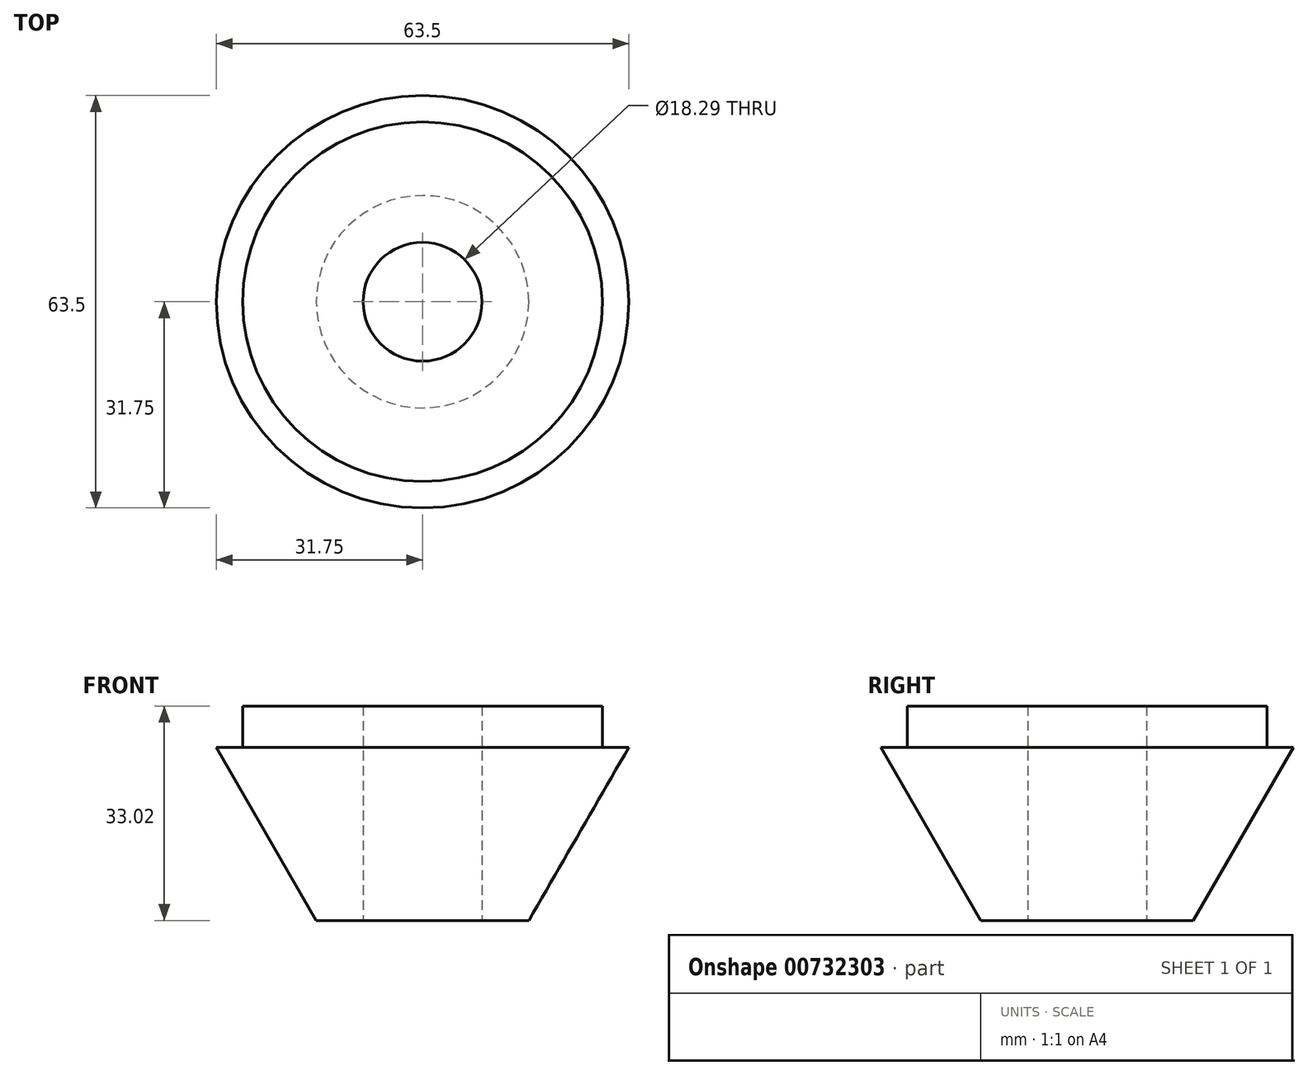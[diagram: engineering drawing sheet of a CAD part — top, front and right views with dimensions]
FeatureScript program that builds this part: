
annotation { "Feature Type Name" : "Feature", "Feature Type Description" : "" }
export const myFeature = defineFeature(function(context is Context, id is Id, definition is map)
    precondition{}
    {
        {
            var Q0;
            Q0=qCreatedBy(makeId("Top.planeOp"),FACE);
            var sketch = newSketch(context, id + "F0", { "sketchPlane" : qUnion([Q0])});
            skCircle(sketch, "E0", {"center": v(0, 0) * mm, "radius": 27.69 * mm});
            skSolve(sketch);
        }
        {
            var Q0;
            Q0=makeQuery(id+"F0.imprint","IMPRINT",FACE,{"disambiguationData":[TD([[makeQuery(id+"F0.imprint","IMPRINT",EDGE,{"derivedFrom":sQuery(id+"F0.wireOp",EDGE,"E0")}),1.0]])]});
            extrude(context, id + "F1", {"entities" : qUnion([Q0]), "depth" : 6.35 * mm, "offsetDistance" : 25.4 * mm});
        }
        {
            var Q0;
            Q0=sQuery(id+"F0.wireOp",VERTEX,"E0.center");
            var Q1;
            Q1=makeQuery(id+"F1.opExtrude","SWEPT_BODY",BODY,{"disambiguationData":[OSD([sQuery(id+"F0.wireOp",EDGE,"E0")])]});
            hole(context, id + "F2", {"style" : HoleStyle.SIMPLE, "endStyle" : HoleEndStyle.THROUGH, "oppositeDirection" : true, "holeDiameter" : 18.29 * mm, "majorDiameter" : 6.35 * mm, "isTappedThrough" : true, "tappedDepth" : 12.7 * mm, "tapClearance" : 3, "locations" : qUnion([Q0]), "scope" : qUnion([Q1])});
        }
        {
            var Q0;
            Q0=qCreatedBy(makeId("Top.planeOp"),FACE);
            var sketch = newSketch(context, id + "F3", { "sketchPlane" : qUnion([Q0])});
            skCircle(sketch, "E1", {"center": v(0, 0) * mm, "radius": 31.75 * mm});
            skSolve(sketch);
        }
        {
            var Q0;
            Q0=qCreatedBy(makeId("Top.planeOp"),FACE);
            cPlane(context, id + "F4", {"entities" : qUnion([Q0]), "cplaneType" : CPlaneType.OFFSET, "offset" : 26.67 * mm, "oppositeDirection" : true, "width" : 152.4 * mm, "height" : 152.4 * mm});
        }
        {
            var Q0;
            Q0=qSketchRegion(id+"F3",true);
            extrude(context, id + "F5", {"entities" : qUnion([Q0]), "operationType" : NewBodyOperationType.ADD, "oppositeDirection" : true, "depth" : 26.67 * mm, "offsetDistance" : 25.4 * mm, "hasDraft" : true, "draftAngle" : 30 * degree, "draftPullDirection" : true});
        }
        {
            var Q0;
            Q0=qCreatedBy(id+"F4.planeOp",FACE);
            var sketch = newSketch(context, id + "F6", { "sketchPlane" : qUnion([Q0])});
            skPoint(sketch, "E2", {"position": v(0, 0) * mm});
            skSolve(sketch);
        }
        {
            var Q0;
            Q0=sQuery(id+"F6.wireOp",VERTEX,"E2");
            var Q1;
            Q1=makeQuery(id+"F1.opExtrude","SWEPT_BODY",BODY,{"disambiguationData":[OSD([sQuery(id+"F0.wireOp",EDGE,"E0")])]});
            hole(context, id + "F7", {"style" : HoleStyle.SIMPLE, "endStyle" : HoleEndStyle.THROUGH, "oppositeDirection" : true, "holeDiameter" : 18.29 * mm, "majorDiameter" : 6.35 * mm, "isTappedThrough" : true, "tappedDepth" : 12.7 * mm, "tapClearance" : 3, "locations" : qUnion([Q0]), "scope" : qUnion([Q1])});
        }
    });
